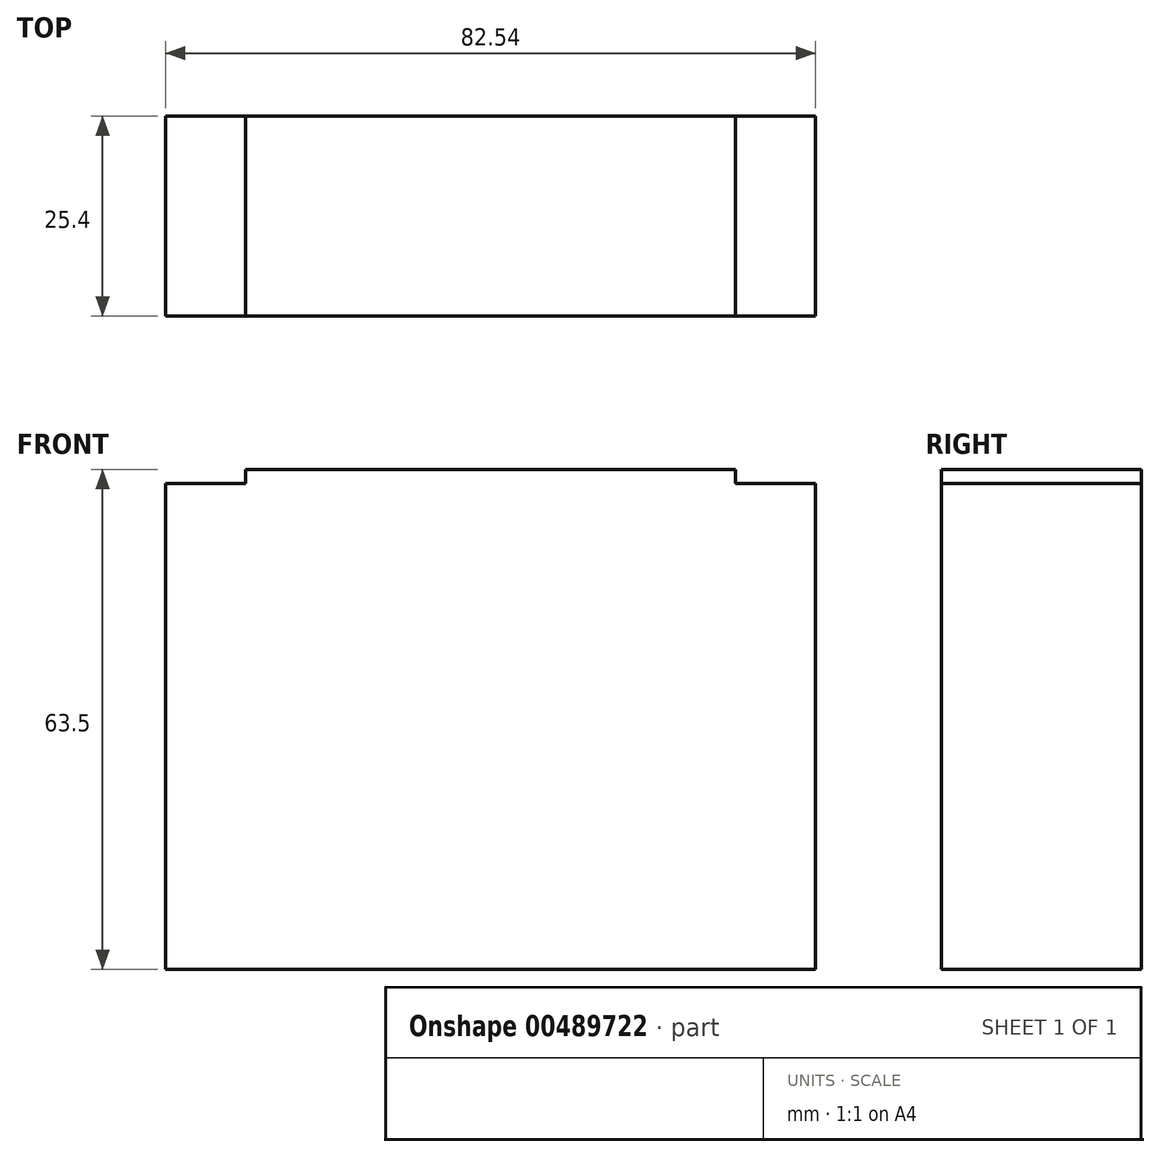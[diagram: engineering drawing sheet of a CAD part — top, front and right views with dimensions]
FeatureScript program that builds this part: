
annotation { "Feature Type Name" : "Feature", "Feature Type Description" : "" }
export const myFeature = defineFeature(function(context is Context, id is Id, definition is map)
    precondition{}
    {
        {
            var Q0;
            Q0=qCreatedBy(makeId("Front.planeOp"),FACE);
            var sketch = newSketch(context, id + "F0", { "sketchPlane" : qUnion([Q0])});
            skLineSegment(sketch, "E0.bottom", {"start": v(31.11, 31.75) * mm, "end": v(-31.12, 31.75) * mm});
            skLineSegment(sketch, "E0.top", {"start": v(41.28, -31.75) * mm, "end": v(-41.28, -31.75) * mm});
            skLineSegment(sketch, "E0.left", {"start": v(41.28, 29.97) * mm, "end": v(41.28, -31.75) * mm});
            skLineSegment(sketch, "E0.right", {"start": v(-41.28, 29.97) * mm, "end": v(-41.28, -31.75) * mm});
            skPoint(sketch, "E0.middle", {"position": v(0, 0) * mm});
            skLineSegment(sketch, "E1.top", {"start": v(-41.28, 29.97) * mm, "end": v(-31.12, 29.97) * mm});
            skLineSegment(sketch, "E1.right", {"start": v(-31.12, 31.75) * mm, "end": v(-31.12, 29.97) * mm});
            skLineSegment(sketch, "E2.top", {"start": v(41.27, 29.97) * mm, "end": v(31.11, 29.97) * mm});
            skLineSegment(sketch, "E2.right", {"start": v(31.11, 31.75) * mm, "end": v(31.11, 29.97) * mm});
            skPoint(sketch, "E3.orphan", {"position": v(-41.28, 31.75) * mm});
            skPoint(sketch, "E4.orphan", {"position": v(41.28, 31.75) * mm});
            skSolve(sketch);
        }
        {
            var Q0;
            Q0 = qSketchRegion(id + "F0", true);
            extrude(context, id + "F1", {"entities" : qUnion([Q0]), "depth" : 25.4 * mm});
        }
    });
